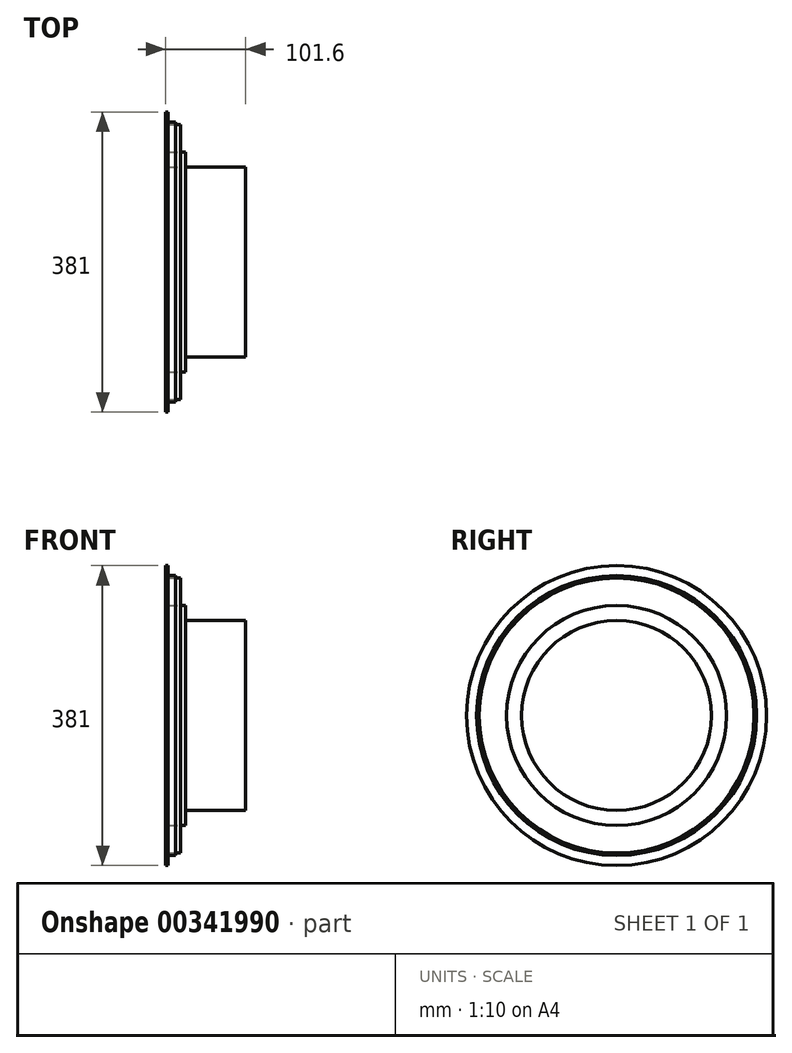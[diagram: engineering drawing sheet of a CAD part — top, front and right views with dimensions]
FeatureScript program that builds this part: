
annotation { "Feature Type Name" : "Feature", "Feature Type Description" : "" }
export const myFeature = defineFeature(function(context is Context, id is Id, definition is map)
    precondition{}
    {
        {
            var Q0;
            Q0=qCreatedBy(makeId("Right.planeOp"),FACE);
            var sketch = newSketch(context, id + "F0", { "sketchPlane" : qUnion([Q0])});
            skCircle(sketch, "E0", {"center": v(0, 0) * mm, "radius": 190.5 * mm});
            skSolve(sketch);
        }
        {
            var Q0;
            Q0=makeQuery(id+"F0.imprint","IMPRINT",FACE,{"disambiguationData":[TD([[makeQuery(id+"F0.imprint","IMPRINT",EDGE,{"derivedFrom":sQuery(id+"F0.wireOp",EDGE,"E0")}),1.0]])]});
            var sketch = newSketch(context, id + "F1", { "sketchPlane" : qUnion([Q0])});
            skCircle(sketch, "E1", {"center": v(0, 0) * mm, "radius": 177.8 * mm});
            skSolve(sketch);
        }
        {
            var Q0;
            Q0=makeQuery(id+"F0.imprint","IMPRINT",FACE,{"disambiguationData":[TD([[makeQuery(id+"F0.imprint","IMPRINT",EDGE,{"derivedFrom":sQuery(id+"F0.wireOp",EDGE,"E0")}),1.0]])]});
            var sketch = newSketch(context, id + "F2", { "sketchPlane" : qUnion([Q0])});
            skCircle(sketch, "E2", {"center": v(0, 0) * mm, "radius": 174.63 * mm});
            skSolve(sketch);
        }
        {
            var Q0;
            Q0=makeQuery(id+"F0.imprint","IMPRINT",FACE,{"disambiguationData":[TD([[makeQuery(id+"F0.imprint","IMPRINT",EDGE,{"derivedFrom":sQuery(id+"F0.wireOp",EDGE,"E0")}),1.0]])]});
            var sketch = newSketch(context, id + "F3", { "sketchPlane" : qUnion([Q0])});
            skCircle(sketch, "E3", {"center": v(0, 0) * mm, "radius": 139.7 * mm});
            skSolve(sketch);
        }
        {
            var Q0;
            Q0=makeQuery(id+"F0.imprint","IMPRINT",FACE,{"disambiguationData":[TD([[makeQuery(id+"F0.imprint","IMPRINT",EDGE,{"derivedFrom":sQuery(id+"F0.wireOp",EDGE,"E0")}),1.0]])]});
            var sketch = newSketch(context, id + "F4", { "sketchPlane" : qUnion([Q0])});
            skCircle(sketch, "E4", {"center": v(0, 0) * mm, "radius": 120.65 * mm});
            skSolve(sketch);
        }
        {
            var Q0;
            Q0=sQuery(id+"F4.wireOp",EDGE,"E4");
            extrude(context, id + "F5", {"bodyType" : ToolBodyType.SURFACE, "surfaceEntities" : qUnion([Q0]), "depth" : 101.6 * mm});
        }
        {
            var Q0;
            Q0=sQuery(id+"F3.wireOp",EDGE,"E3");
            extrude(context, id + "F6", {"bodyType" : ToolBodyType.SURFACE, "surfaceEntities" : qUnion([Q0]), "depth" : 25.4 * mm});
        }
        {
            var Q0;
            Q0=sQuery(id+"F2.wireOp",EDGE,"E2");
            extrude(context, id + "F7", {"bodyType" : ToolBodyType.SURFACE, "surfaceEntities" : qUnion([Q0]), "depth" : 19.05 * mm});
        }
        {
            var Q0;
            Q0=sQuery(id+"F1.wireOp",EDGE,"E1");
            extrude(context, id + "F8", {"bodyType" : ToolBodyType.SURFACE, "surfaceEntities" : qUnion([Q0]), "depth" : 12.7 * mm});
        }
        {
            var Q0;
            Q0=sQuery(id+"F0.wireOp",EDGE,"E0");
            extrude(context, id + "F9", {"bodyType" : ToolBodyType.SURFACE, "surfaceEntities" : qUnion([Q0]), "depth" : 3.17 * mm});
        }
    });
